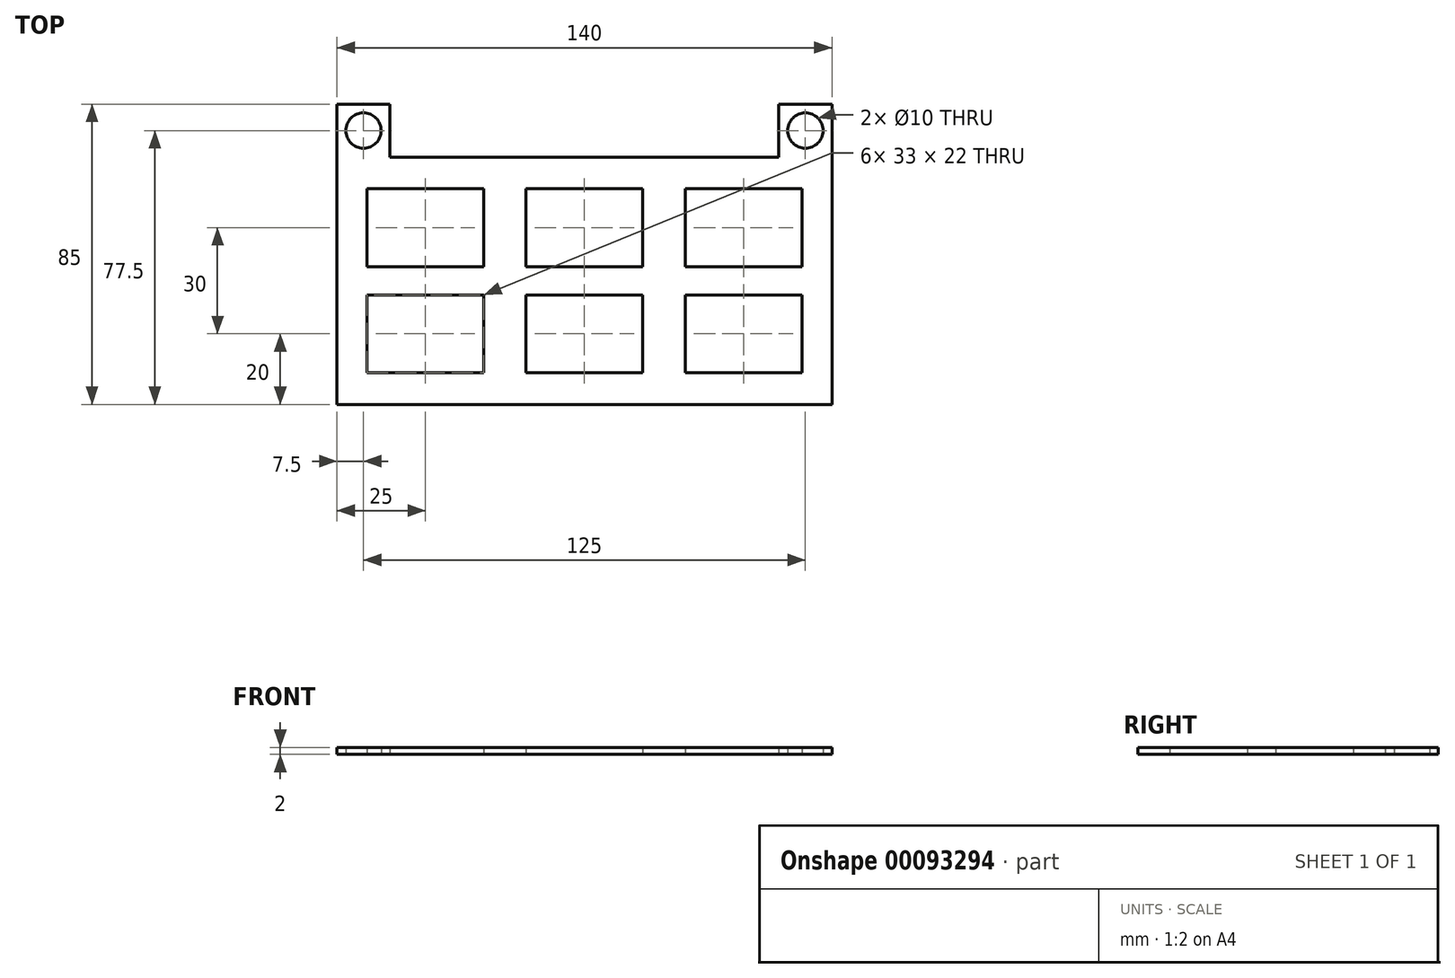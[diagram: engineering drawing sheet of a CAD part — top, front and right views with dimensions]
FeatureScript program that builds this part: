
annotation { "Feature Type Name" : "Feature", "Feature Type Description" : "" }
export const myFeature = defineFeature(function(context is Context, id is Id, definition is map)
    precondition{}
    {
        {
            var Q0;
            Q0=qCreatedBy(makeId("Top.planeOp"),FACE);
            var sketch = newSketch(context, id + "F0", { "sketchPlane" : qUnion([Q0])});
            skLineSegment(sketch, "E0.bottom", {"start": v(0, 0) * mm, "end": v(140, 0) * mm});
            skLineSegment(sketch, "E0.top", {"start": v(15, 70) * mm, "end": v(125, 70) * mm});
            skLineSegment(sketch, "E0.left", {"start": v(0, 0) * mm, "end": v(0, 70) * mm});
            skLineSegment(sketch, "E0.right", {"start": v(140, 0) * mm, "end": v(140, 70) * mm});
            skLineSegment(sketch, "E1.bottom", {"start": v(8.5, 9) * mm, "end": v(41.5, 9) * mm});
            skLineSegment(sketch, "E1.top", {"start": v(8.5, 31) * mm, "end": v(41.5, 31) * mm});
            skLineSegment(sketch, "E1.left", {"start": v(8.5, 9) * mm, "end": v(8.5, 31) * mm});
            skLineSegment(sketch, "E1.right", {"start": v(41.5, 9) * mm, "end": v(41.5, 31) * mm});
            skLineSegment(sketch, "E2.0.1.0", {"start": v(8.5, 61) * mm, "end": v(41.5, 61) * mm});
            skLineSegment(sketch, "E2.0.1.1", {"start": v(8.5, 39) * mm, "end": v(8.5, 61) * mm});
            skLineSegment(sketch, "E2.0.1.2", {"start": v(41.5, 39) * mm, "end": v(41.5, 61) * mm});
            skLineSegment(sketch, "E2.0.1.3", {"start": v(8.5, 39) * mm, "end": v(41.5, 39) * mm});
            skLineSegment(sketch, "E2.1.0.0", {"start": v(53.5, 31) * mm, "end": v(86.5, 31) * mm});
            skLineSegment(sketch, "E2.1.0.1", {"start": v(53.5, 9) * mm, "end": v(53.5, 31) * mm});
            skLineSegment(sketch, "E2.1.0.2", {"start": v(86.5, 9) * mm, "end": v(86.5, 31) * mm});
            skLineSegment(sketch, "E2.1.0.3", {"start": v(53.5, 9) * mm, "end": v(86.5, 9) * mm});
            skLineSegment(sketch, "E2.1.1.0", {"start": v(53.5, 61) * mm, "end": v(86.5, 61) * mm});
            skLineSegment(sketch, "E2.1.1.1", {"start": v(53.5, 39) * mm, "end": v(53.5, 61) * mm});
            skLineSegment(sketch, "E2.1.1.2", {"start": v(86.5, 39) * mm, "end": v(86.5, 61) * mm});
            skLineSegment(sketch, "E2.1.1.3", {"start": v(53.5, 39) * mm, "end": v(86.5, 39) * mm});
            skLineSegment(sketch, "E2.2.0.0", {"start": v(98.5, 31) * mm, "end": v(131.5, 31) * mm});
            skLineSegment(sketch, "E2.2.0.1", {"start": v(98.5, 9) * mm, "end": v(98.5, 31) * mm});
            skLineSegment(sketch, "E2.2.0.2", {"start": v(131.5, 9) * mm, "end": v(131.5, 31) * mm});
            skLineSegment(sketch, "E2.2.0.3", {"start": v(98.5, 9) * mm, "end": v(131.5, 9) * mm});
            skLineSegment(sketch, "E2.2.1.0", {"start": v(98.5, 61) * mm, "end": v(131.5, 61) * mm});
            skLineSegment(sketch, "E2.2.1.1", {"start": v(98.5, 39) * mm, "end": v(98.5, 61) * mm});
            skLineSegment(sketch, "E2.2.1.2", {"start": v(131.5, 39) * mm, "end": v(131.5, 61) * mm});
            skLineSegment(sketch, "E2.2.1.3", {"start": v(98.5, 39) * mm, "end": v(131.5, 39) * mm});
            skLineSegment(sketch, "E2.direction1", {"start": v(8.5, 31) * mm, "end": v(53.5, 31) * mm, "construction": true});
            skLineSegment(sketch, "E2.direction2", {"start": v(8.5, 31) * mm, "end": v(8.5, 61) * mm, "construction": true});
            skLineSegment(sketch, "E3", {"start": v(70, 92.5) * mm, "end": v(70, -29.34) * mm, "construction": true});
            skLineSegment(sketch, "E4", {"start": v(0, 70) * mm, "end": v(0, 85) * mm});
            skLineSegment(sketch, "E5", {"start": v(0, 85) * mm, "end": v(15, 85) * mm});
            skLineSegment(sketch, "E6", {"start": v(15, 85) * mm, "end": v(15, 70) * mm});
            skLineSegment(sketch, "E7", {"start": v(-8.73, 35) * mm, "end": v(157.26, 35) * mm, "construction": true});
            skLineSegment(sketch, "E8.MirrorCS", {"start": v(125, 85) * mm, "end": v(125, 70) * mm});
            skLineSegment(sketch, "E9.MirrorCS", {"start": v(140, 85) * mm, "end": v(125, 85) * mm});
            skLineSegment(sketch, "E10.MirrorCS", {"start": v(140, 70) * mm, "end": v(140, 85) * mm});
            skCircle(sketch, "E11", {"center": v(7.5, 77.5) * mm, "radius": 5 * mm});
            skPoint(sketch, "E11.centerSnap0", {"position": v(7.5, 85) * mm});
            skPoint(sketch, "E11.centerSnap1", {"position": v(0, 77.5) * mm});
            skCircle(sketch, "E12.MirrorC", {"center": v(132.5, 77.5) * mm, "radius": 5 * mm});
            skSolve(sketch);
        }
        {
            var Q0;
            Q0=makeQuery(id+"F0.imprint","IMPRINT",FACE,{"disambiguationData":[TD([[makeQuery(id+"F0.imprint","IMPRINT",EDGE,{"derivedFrom":sQuery(id+"F0.wireOp",EDGE,"E0.bottom")}),1.0]])]});
            extrude(context, id + "F1", {"entities" : qUnion([Q0]), "depth" : 2 * mm});
        }
    });
